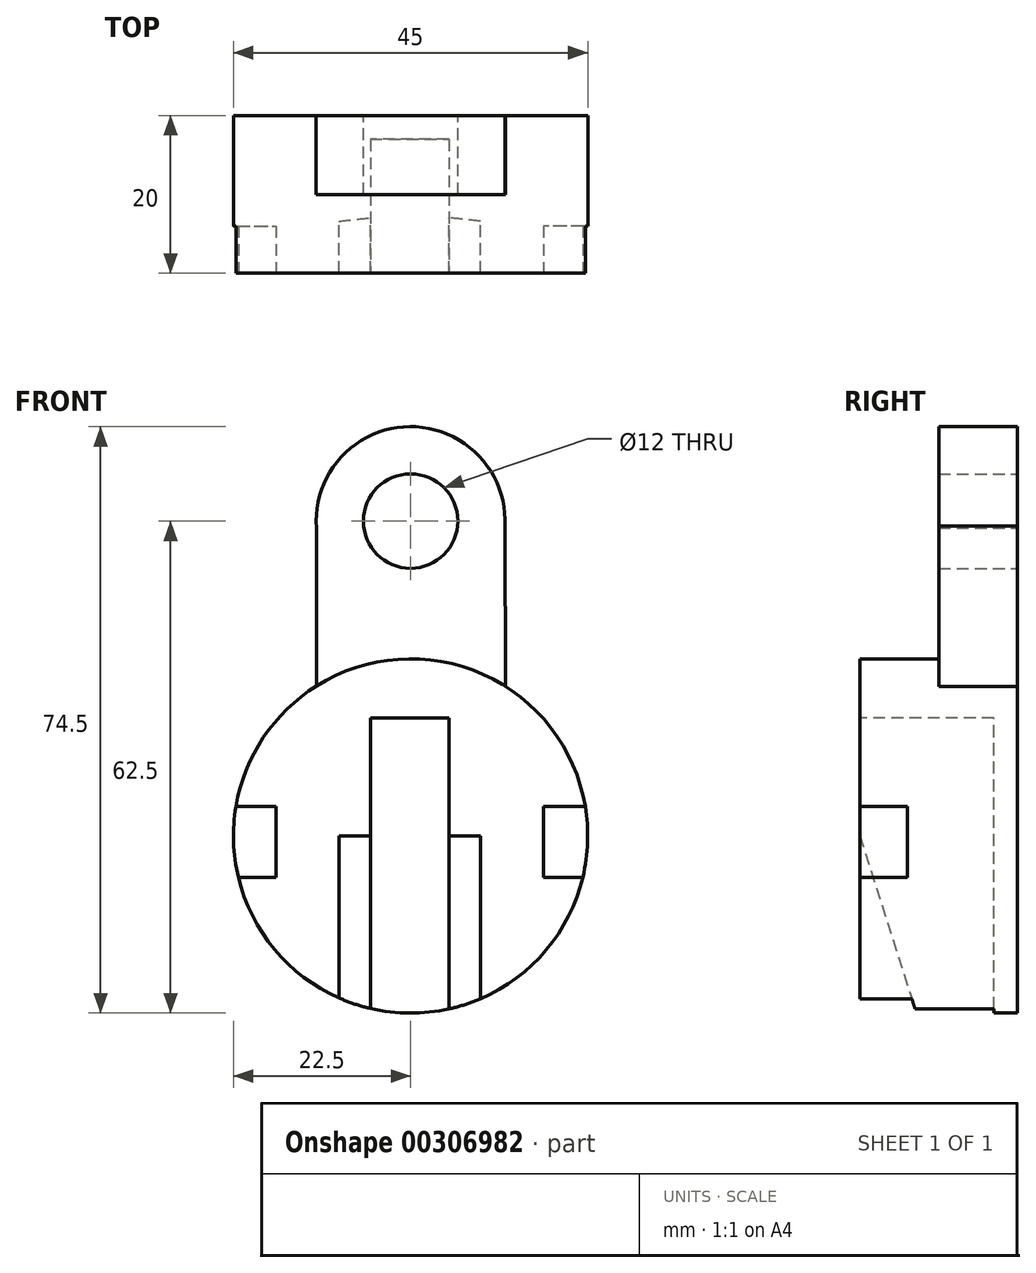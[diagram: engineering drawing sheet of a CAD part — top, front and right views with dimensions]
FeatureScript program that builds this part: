
annotation { "Feature Type Name" : "Feature", "Feature Type Description" : "" }
export const myFeature = defineFeature(function(context is Context, id is Id, definition is map)
    precondition{}
    {
        {
            var Q0;
            Q0=qCreatedBy(makeId("Front.planeOp"),FACE);
            var sketch = newSketch(context, id + "F0", { "sketchPlane" : qUnion([Q0])});
            skCircle(sketch, "E0", {"center": v(0, 0) * mm, "radius": 22.5 * mm});
            skSolve(sketch);
        }
        {
            var Q0;
            Q0=makeQuery(id+"F0.imprint","IMPRINT",FACE,{"disambiguationData":[TD([[makeQuery(id+"F0.imprint","IMPRINT",EDGE,{"derivedFrom":sQuery(id+"F0.wireOp",EDGE,"E0")}),1.0]])]});
            extrude(context, id + "F1", {"entities" : qUnion([Q0]), "depth" : 20 * mm});
        }
        {
            var Q0;
            Q0=makeQuery(id+"F1.opExtrude","CAP_FACE",FACE,{"disambiguationData":[OSD([sQuery(id+"F0.wireOp",EDGE,"E0")])],"isStart":false});
            var sketch = newSketch(context, id + "F2", { "sketchPlane" : qUnion([Q0])});
            skLineSegment(sketch, "E1.bottom", {"start": v(22.89, 3.76) * mm, "end": v(16.89, 3.76) * mm});
            skLineSegment(sketch, "E1.top", {"start": v(22.89, -5.24) * mm, "end": v(16.89, -5.24) * mm});
            skLineSegment(sketch, "E1.left", {"start": v(22.89, 3.76) * mm, "end": v(22.89, -5.24) * mm});
            skLineSegment(sketch, "E1.right", {"start": v(16.89, 3.76) * mm, "end": v(16.89, -5.24) * mm});
            skPoint(sketch, "E2.oppositeSnap0", {"position": v(19.89, -5.24) * mm});
            skLineSegment(sketch, "E2.bottom", {"start": v(-17.11, 3.76) * mm, "end": v(-19.68, 3.76) * mm});
            skLineSegment(sketch, "E2.top", {"start": v(-17.11, -5.24) * mm, "end": v(-19.68, -5.24) * mm});
            skLineSegment(sketch, "E2.left", {"start": v(-17.11, 3.76) * mm, "end": v(-17.11, -5.24) * mm});
            skLineSegment(sketch, "E2.right", {"start": v(-19.68, 3.76) * mm, "end": v(-19.68, -5.24) * mm});
            skLineSegment(sketch, "E3.MirrorCS", {"start": v(-22.89, 3.76) * mm, "end": v(-16.89, 3.76) * mm});
            skLineSegment(sketch, "E4.MirrorCS", {"start": v(-22.89, -5.24) * mm, "end": v(-16.89, -5.24) * mm});
            skLineSegment(sketch, "E5.MirrorCS", {"start": v(-22.89, 3.76) * mm, "end": v(-22.89, -5.24) * mm});
            skSolve(sketch);
        }
        {
            var Q0;
            {var subQ0=sQuery(id+"F2.wireOp",EDGE,"E2.right");Q0=makeQuery(id+"F2.imprint","IMPRINT",FACE,{"disambiguationData":[TD([[makeQuery(id+"F2.imprint","IMPRINT",EDGE,{"derivedFrom":subQ0}),-1.0]])]});}
            var Q1;
            {var subQ0=sQuery(id+"F2.wireOp",EDGE,"E2.left");Q1=makeQuery(id+"F2.imprint","IMPRINT",FACE,{"disambiguationData":[TD([[makeQuery(id+"F2.imprint","IMPRINT",EDGE,{"derivedFrom":subQ0}),-1.0]])]});}
            var Q2;
            {var subQ0=sQuery(id+"F2.wireOp",EDGE,"E1.right");Q2=makeQuery(id+"F2.imprint","IMPRINT",FACE,{"disambiguationData":[TD([[makeQuery(id+"F2.imprint","IMPRINT",EDGE,{"derivedFrom":subQ0}),1.0]])]});}
            extrude(context, id + "F3", {"entities" : qUnion([Q0, Q1, Q2]), "operationType" : NewBodyOperationType.REMOVE, "oppositeDirection" : true, "depth" : 6 * mm});
        }
        {
            var Q0;
            Q0=makeQuery(id+"F1.opExtrude","CAP_FACE",FACE,{"disambiguationData":[OSD([sQuery(id+"F0.wireOp",EDGE,"E0")])],"isStart":false});
            var sketch = newSketch(context, id + "F4", { "sketchPlane" : qUnion([Q0])});
            skLineSegment(sketch, "E6.bottom", {"start": v(4.89, -140) * mm, "end": v(-5.11, -140) * mm});
            skLineSegment(sketch, "E6.top", {"start": v(4.89, 15) * mm, "end": v(-5.11, 15) * mm});
            skLineSegment(sketch, "E6.left", {"start": v(4.89, -140) * mm, "end": v(4.89, 15) * mm});
            skLineSegment(sketch, "E6.right", {"start": v(-5.11, -140) * mm, "end": v(-5.11, 15) * mm});
            skSolve(sketch);
        }
        {
            var Q0;
            {var subQ0=sQuery(id+"F4.wireOp",EDGE,"E6.top");Q0=makeQuery(id+"F4.imprint","IMPRINT",FACE,{"disambiguationData":[TD([[makeQuery(id+"F4.imprint","IMPRINT",EDGE,{"derivedFrom":subQ0}),1.0]])]});}
            extrude(context, id + "F5", {"entities" : qUnion([Q0]), "operationType" : NewBodyOperationType.REMOVE, "oppositeDirection" : true, "depth" : 17 * mm});
        }
        {
            var Q0;
            Q0=makeQuery(id+"F5.boolean.opBoolean","COPY",FACE,{"derivedFrom":makeQuery(id+"F5.opExtrude","SWEPT_FACE",FACE,{"disambiguationData":[OSD([sQuery(id+"F4.wireOp",EDGE,"E6.left")])]})});
            var sketch = newSketch(context, id + "F6", { "sketchPlane" : qUnion([Q0])});
            skLineSegment(sketch, "E7", {"start": v(13, -21.96) * mm, "end": v(20, -21.96) * mm});
            skLineSegment(sketch, "E8", {"start": v(20, -21.96) * mm, "end": v(20, 0) * mm});
            skLineSegment(sketch, "E9", {"start": v(20, 0) * mm, "end": v(13, -21.96) * mm});
            skSolve(sketch);
        }
        {
            var Q0;
            Q0=makeQuery(id+"F6.imprint","IMPRINT",FACE,{"disambiguationData":[TD([[makeQuery(id+"F6.imprint","IMPRINT",EDGE,{"derivedFrom":sQuery(id+"F6.wireOp",EDGE,"E7")}),1.0]])]});
            extrude(context, id + "F7", {"entities" : qUnion([Q0]), "operationType" : NewBodyOperationType.REMOVE, "oppositeDirection" : true, "depth" : 4 * mm});
        }
        {
            var Q0;
            Q0=makeQuery(id+"F5.boolean.opBoolean","COPY",FACE,{"derivedFrom":makeQuery(id+"F5.opExtrude","SWEPT_FACE",FACE,{"disambiguationData":[OSD([sQuery(id+"F4.wireOp",EDGE,"E6.right")])]})});
            var sketch = newSketch(context, id + "F8", { "sketchPlane" : qUnion([Q0])});
            skLineSegment(sketch, "E10", {"start": v(-13, -21.91) * mm, "end": v(-20, -21.91) * mm});
            skLineSegment(sketch, "E11", {"start": v(-20, -21.91) * mm, "end": v(-20, 0) * mm});
            skLineSegment(sketch, "E12", {"start": v(-20, 0) * mm, "end": v(-13, -21.91) * mm});
            skSolve(sketch);
        }
        {
            var Q0;
            Q0=makeQuery(id+"F8.imprint","IMPRINT",FACE,{"disambiguationData":[TD([[makeQuery(id+"F8.imprint","IMPRINT",EDGE,{"derivedFrom":sQuery(id+"F8.wireOp",EDGE,"E10")}),-1.0]])]});
            extrude(context, id + "F9", {"entities" : qUnion([Q0]), "operationType" : NewBodyOperationType.REMOVE, "oppositeDirection" : true, "depth" : 4 * mm});
        }
        {
            var Q0;
            Q0=qCreatedBy(makeId("Front.planeOp"),FACE);
            var sketch = newSketch(context, id + "F10", { "sketchPlane" : qUnion([Q0])});
            skCircle(sketch, "E13", {"center": v(0, 40) * mm, "radius": 6 * mm});
            skCircle(sketch, "E14", {"center": v(0, 40) * mm, "radius": 12 * mm});
            skLineSegment(sketch, "E15", {"start": v(-11.97, 39.15) * mm, "end": v(-11.97, 18.84) * mm});
            skLineSegment(sketch, "E16", {"start": v(-11.97, 18.84) * mm, "end": v(12.03, 18.84) * mm});
            skLineSegment(sketch, "E17", {"start": v(12.03, 18.84) * mm, "end": v(11.98, 39.34) * mm});
            skLineSegment(sketch, "E18", {"start": v(-11.97, 39.15) * mm, "end": v(11.98, 39.34) * mm});
            skSolve(sketch);
        }
        {
            var Q0;
            {var subQ1=sQuery(id+"F10.wireOp",EDGE,"E15");Q0=makeQuery(id+"F10.imprint","IMPRINT",FACE,{"disambiguationData":[TD([[makeQuery(id+"F10.imprint","IMPRINT",EDGE,{"derivedFrom":subQ1}),1.0]])]});}
            var Q1;
            {var subQ0=sQuery(id+"F10.wireOp",EDGE,"E18");var subQ1=sQuery(id+"F10.wireOp",EDGE,"E13");var subQ2=makeQuery(id+"F10.imprint","INTERSECT",VERTEX,{"disambiguationData":[OD(0.0)],"derivedFrom":[subQ1,subQ0]});Q1=makeQuery(id+"F10.imprint","IMPRINT",FACE,{"disambiguationData":[TD([[makeQuery(id+"F10.imprint","IMPRINT",EDGE,{"disambiguationData":[TD([[subQ2,-1.0]])],"derivedFrom":subQ1}),-1.0]])]});}
            var Q2;
            {var subQ0=sQuery(id+"F10.wireOp",EDGE,"E18");var subQ1=sQuery(id+"F10.wireOp",EDGE,"E13");var subQ2=makeQuery(id+"F10.imprint","INTERSECT",VERTEX,{"disambiguationData":[OD(0.0)],"derivedFrom":[subQ1,subQ0]});Q2=makeQuery(id+"F10.imprint","IMPRINT",FACE,{"disambiguationData":[TD([[makeQuery(id+"F10.imprint","IMPRINT",EDGE,{"disambiguationData":[TD([[subQ2,1.0]])],"derivedFrom":subQ1}),-1.0]])]});}
            extrude(context, id + "F11", {"entities" : qUnion([Q0, Q1, Q2]), "operationType" : NewBodyOperationType.ADD, "depth" : 10 * mm});
        }
    });
